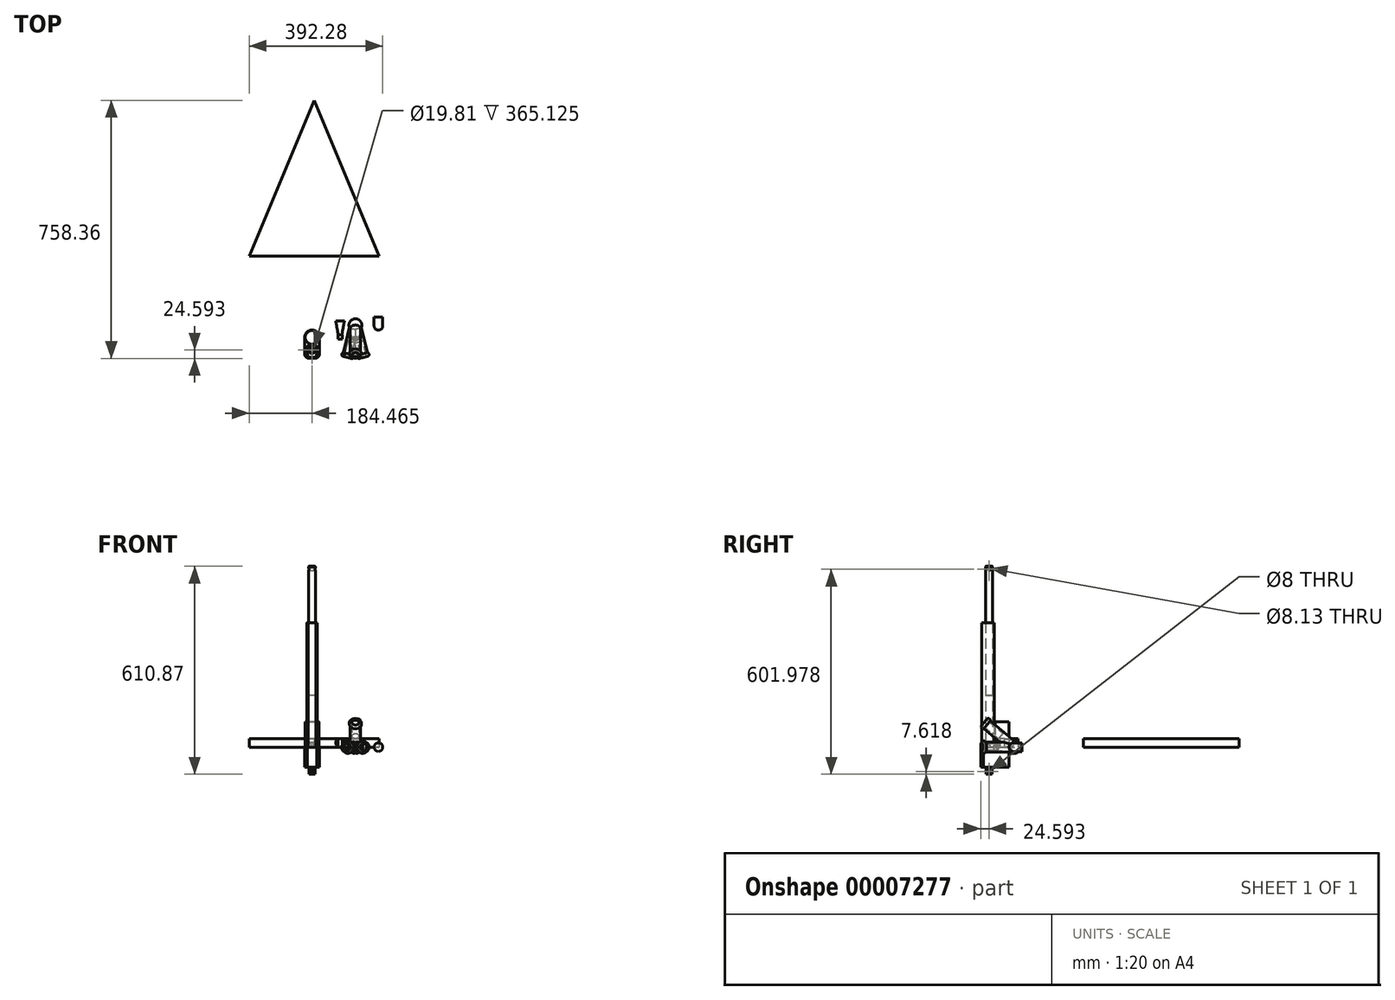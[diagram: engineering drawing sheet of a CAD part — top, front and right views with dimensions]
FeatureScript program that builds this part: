
annotation { "Feature Type Name" : "Feature", "Feature Type Description" : "" }
export const myFeature = defineFeature(function(context is Context, id is Id, definition is map)
    precondition{}
    {
        {
            var Q0;
            Q0=qCreatedBy(makeId("Top.planeOp"),FACE);
            var sketch = newSketch(context, id + "F0", { "sketchPlane" : qUnion([Q0])});
            skLineSegment(sketch, "E0", {"start": v(-190.5, -762.12) * mm, "end": v(0, 0) * mm});
            skLineSegment(sketch, "E1", {"start": v(0, 0) * mm, "end": v(190.5, -762.12) * mm});
            skLineSegment(sketch, "E2", {"start": v(-190.5, -762.12) * mm, "end": v(190.5, -762.12) * mm, "construction": true});
            skPoint(sketch, "E3", {"position": v(0, -762.12) * mm});
            skLineSegment(sketch, "E4.rect.bottom", {"start": v(-48.64, -235.45) * mm, "end": v(-67.86, -230.64) * mm});
            skLineSegment(sketch, "E4.rect.top", {"start": v(-2.54, -51.01) * mm, "end": v(-21.76, -46.2) * mm});
            skLineSegment(sketch, "E4.rect.left", {"start": v(-48.64, -235.45) * mm, "end": v(-2.54, -51.01) * mm});
            skLineSegment(sketch, "E4.rect.right", {"start": v(-67.86, -230.64) * mm, "end": v(-21.76, -46.2) * mm});
            skPoint(sketch, "E4.rect.middle", {"position": v(-35.2, -140.83) * mm});
            skLineSegment(sketch, "E5.rect.bottom", {"start": v(65.5, -221.22) * mm, "end": v(46.29, -226.03) * mm});
            skLineSegment(sketch, "E5.rect.top", {"start": v(21.76, -46.2) * mm, "end": v(2.54, -51.01) * mm});
            skLineSegment(sketch, "E5.rect.left", {"start": v(65.5, -221.22) * mm, "end": v(21.76, -46.2) * mm});
            skLineSegment(sketch, "E5.rect.right", {"start": v(46.29, -226.03) * mm, "end": v(2.54, -51.01) * mm});
            skPoint(sketch, "E5.rect.middle", {"position": v(34.02, -136.12) * mm});
            skCircle(sketch, "E6", {"center": v(0, 0) * mm, "radius": 19.05 * mm});
            skLineSegment(sketch, "E7", {"start": v(-7.7, -92.6) * mm, "end": v(0, -61.8) * mm});
            skLineSegment(sketch, "E8", {"start": v(0, -61.8) * mm, "end": v(7.7, -92.6) * mm});
            skLineSegment(sketch, "E9", {"start": v(-36.78, -85.33) * mm, "end": v(-31.85, -86.56) * mm});
            skLineSegment(sketch, "E10", {"start": v(7.7, -92.6) * mm, "end": v(31.85, -86.56) * mm});
            skLineSegment(sketch, "E11", {"start": v(0, -61.8) * mm, "end": v(0, 0) * mm});
            skLineSegment(sketch, "E12", {"start": v(-3.81, -56.1) * mm, "end": v(1.11, -57.34) * mm});
            skLineSegment(sketch, "E13", {"start": v(8.21, -94.65) * mm, "end": v(13.14, -93.42) * mm, "construction": true});
            skLineSegment(sketch, "E14", {"start": v(36.78, -85.33) * mm, "end": v(17.4, -7.78) * mm});
            skLineSegment(sketch, "E15", {"start": v(-36.78, -85.33) * mm, "end": v(-17.4, -7.78) * mm});
            skLineSegment(sketch, "E16", {"start": v(-25.07, -59.45) * mm, "end": v(-30, -58.22) * mm, "construction": true});
            skLineSegment(sketch, "E17", {"start": v(28.15, -71.75) * mm, "end": v(33.07, -70.52) * mm, "construction": true});
            skLineSegment(sketch, "E18", {"start": v(0, 0) * mm, "end": v(0, 19.05) * mm});
            skCircle(sketch, "E19", {"center": v(-34.31, -85.95) * mm, "radius": 5.71 * mm});
            skCircle(sketch, "E20", {"center": v(34.31, -85.95) * mm, "radius": 5.71 * mm});
            skLineSegment(sketch, "E21", {"start": v(-31.85, -86.56) * mm, "end": v(-7.7, -92.6) * mm});
            skLineSegment(sketch, "E22", {"start": v(31.85, -86.56) * mm, "end": v(36.78, -85.33) * mm});
            skSolve(sketch);
        }
        {
            var Q0;
            Q0=qCreatedBy(makeId("Right.planeOp"),FACE);
            var sketch = newSketch(context, id + "F1", { "sketchPlane" : qUnion([Q0])});
            skLineSegment(sketch, "E23", {"start": v(0, 0) * mm, "end": v(-762.12, 634.6) * mm});
            skLineSegment(sketch, "E24.rect.bottom", {"start": v(-32.7, 40.12) * mm, "end": v(-45.38, 24.9) * mm});
            skLineSegment(sketch, "E24.rect.top", {"start": v(-267.13, 235.32) * mm, "end": v(-279.8, 220.1) * mm});
            skLineSegment(sketch, "E24.rect.left", {"start": v(-45.38, 24.9) * mm, "end": v(-279.8, 220.1) * mm});
            skLineSegment(sketch, "E24.rect.right", {"start": v(-32.7, 40.12) * mm, "end": v(-267.13, 235.32) * mm});
            skPoint(sketch, "E24.rect.middle", {"position": v(-156.25, 130.1) * mm});
            skCircle(sketch, "E25", {"center": v(0, 0) * mm, "radius": 19.05 * mm});
            skLineSegment(sketch, "E26", {"start": v(0, 0) * mm, "end": v(-246.27, 0) * mm, "construction": true});
            skLineSegment(sketch, "E27", {"start": v(0.55, 19.04) * mm, "end": v(-73.42, 80.64) * mm});
            skLineSegment(sketch, "E28", {"start": v(-73.42, 80.64) * mm, "end": v(-76.67, 76.73) * mm});
            skLineSegment(sketch, "E29", {"start": v(-18.63, -4) * mm, "end": v(-92.6, 57.6) * mm});
            skLineSegment(sketch, "E30", {"start": v(-92.6, 57.6) * mm, "end": v(-89.35, 61.5) * mm});
            skCircle(sketch, "E31", {"center": v(-75.05, 78.69) * mm, "radius": 5.72 * mm});
            skSolve(sketch);
        }
        {
            var Q0;
            {var subQ5=sQuery(id+"F0.wireOp",EDGE,"E9");Q0=makeQuery(id+"F0.imprint","IMPRINT",FACE,{"disambiguationData":[TD([[makeQuery(id+"F0.imprint","IMPRINT",EDGE,{"derivedFrom":subQ5}),1.0]])]});}
            var Q1;
            {var subQ5=sQuery(id+"F0.wireOp",EDGE,"E9");Q1=makeQuery(id+"F0.imprint","IMPRINT",FACE,{"disambiguationData":[TD([[makeQuery(id+"F0.imprint","IMPRINT",EDGE,{"derivedFrom":subQ5}),-1.0]])]});}
            var Q2;
            {var subQ7=sQuery(id+"F0.wireOp",EDGE,"E0");var subQ9=sQuery(id+"F0.wireOp",EDGE,"E4.rect.top");var subQ10=makeQuery(id+"F0.imprint","INTERSECT",VERTEX,{"derivedFrom":[subQ7,subQ9]});Q2=makeQuery(id+"F0.imprint","IMPRINT",FACE,{"disambiguationData":[TD([[makeQuery(id+"F0.imprint","IMPRINT",EDGE,{"disambiguationData":[TD([[subQ10,-1.0]])],"derivedFrom":subQ7}),1.0]])]});}
            var Q3;
            {var subQ0=sQuery(id+"F0.wireOp",EDGE,"E18");Q3=makeQuery(id+"F0.imprint","IMPRINT",FACE,{"disambiguationData":[TD([[makeQuery(id+"F0.imprint","IMPRINT",EDGE,{"derivedFrom":subQ0}),1.0]])]});}
            var Q4;
            Q4=sQuery(id+"F0.wireOp",EDGE,"E0");
            revolve(context, id + "F2", {"entities" : qUnion([Q0, Q1, Q2, Q3]), "axis" : qUnion([Q4]), "revolveType" : RevolveType.FULL});
        }
        {
            var Q0;
            {var subQ5=sQuery(id+"F0.wireOp",EDGE,"E22");Q0=makeQuery(id+"F0.imprint","IMPRINT",FACE,{"disambiguationData":[TD([[makeQuery(id+"F0.imprint","IMPRINT",EDGE,{"derivedFrom":subQ5}),-1.0]])]});}
            var Q1;
            {var subQ5=sQuery(id+"F0.wireOp",EDGE,"E22");Q1=makeQuery(id+"F0.imprint","IMPRINT",FACE,{"disambiguationData":[TD([[makeQuery(id+"F0.imprint","IMPRINT",EDGE,{"derivedFrom":subQ5}),1.0]])]});}
            var Q2;
            {var subQ5=sQuery(id+"F0.wireOp",EDGE,"E1");var subQ8=sQuery(id+"F0.wireOp",EDGE,"E6");var subQ9=makeQuery(id+"F0.imprint","INTERSECT",VERTEX,{"derivedFrom":[subQ5,subQ8]});Q2=makeQuery(id+"F0.imprint","IMPRINT",FACE,{"disambiguationData":[TD([[makeQuery(id+"F0.imprint","IMPRINT",EDGE,{"disambiguationData":[TD([[subQ9,-1.0]])],"derivedFrom":subQ5}),1.0]])]});}
            var Q3;
            {var subQ4=sQuery(id+"F0.wireOp",EDGE,"E18");Q3=makeQuery(id+"F0.imprint","IMPRINT",FACE,{"disambiguationData":[TD([[makeQuery(id+"F0.imprint","IMPRINT",EDGE,{"derivedFrom":subQ4}),-1.0]])]});}
            var Q4;
            Q4=sQuery(id+"F0.wireOp",EDGE,"E1");
            revolve(context, id + "F3", {"operationType" : NewBodyOperationType.ADD, "entities" : qUnion([Q0, Q1, Q2, Q3]), "axis" : qUnion([Q4]), "revolveType" : RevolveType.FULL});
        }
        {
            var Q0;
            {var subQ0=sQuery(id+"F1.wireOp",EDGE,"E28");Q0=makeQuery(id+"F1.imprint","IMPRINT",FACE,{"disambiguationData":[TD([[makeQuery(id+"F1.imprint","IMPRINT",EDGE,{"derivedFrom":subQ0}),1.0]])]});}
            var Q1;
            {var subQ5=sQuery(id+"F1.wireOp",EDGE,"E28");Q1=makeQuery(id+"F1.imprint","IMPRINT",FACE,{"disambiguationData":[TD([[makeQuery(id+"F1.imprint","IMPRINT",EDGE,{"derivedFrom":subQ5}),-1.0]])]});}
            var Q2;
            {var subQ5=sQuery(id+"F1.wireOp",EDGE,"E25");var subQ7=sQuery(id+"F1.wireOp",EDGE,"E23");var subQ10=makeQuery(id+"F1.imprint","INTERSECT",VERTEX,{"derivedFrom":[subQ7,subQ5]});Q2=makeQuery(id+"F1.imprint","IMPRINT",FACE,{"disambiguationData":[TD([[makeQuery(id+"F1.imprint","IMPRINT",EDGE,{"disambiguationData":[TD([[subQ10,-1.0]])],"derivedFrom":subQ7}),-1.0]])]});}
            var Q3;
            Q3=sQuery(id+"F1.wireOp",EDGE,"E23");
            revolve(context, id + "F4", {"operationType" : NewBodyOperationType.ADD, "entities" : qUnion([Q0, Q1, Q2]), "axis" : qUnion([Q3]), "revolveType" : RevolveType.FULL});
        }
        {
            var Q0;
            Q0=qCreatedBy(makeId("Top.planeOp"),FACE);
            var sketch = newSketch(context, id + "F5", { "sketchPlane" : qUnion([Q0])});
            skCircle(sketch, "E32", {"center": v(-127.41, -73.1) * mm, "radius": 9.9 * mm});
            skArc(sketch, "E33", {"start": v(-112.6, -76.12) * mm, "mid": v(-127.41, -58) * mm, "end": v(-142.22, -76.12) * mm});
            skLineSegment(sketch, "E34", {"start": v(-138.47, -94.57) * mm, "end": v(-116.36, -94.57) * mm});
            skLineSegment(sketch, "E35", {"start": v(-116.36, -94.57) * mm, "end": v(-112.6, -76.12) * mm});
            skLineSegment(sketch, "E36", {"start": v(-138.47, -94.57) * mm, "end": v(-142.22, -76.12) * mm});
            skSolve(sketch);
        }
        {
            var Q0;
            Q0=makeQuery(id+"F5.imprint","IMPRINT",FACE,{"disambiguationData":[TD([[makeQuery(id+"F5.imprint","IMPRINT",EDGE,{"derivedFrom":sQuery(id+"F5.wireOp",EDGE,"E32")}),1.0]])]});
            extrude(context, id + "F6", {"entities" : qUnion([Q0]), "depth" : 531.37 * mm});
        }
        {
            var Q0;
            Q0=makeQuery(id+"F5.imprint","IMPRINT",FACE,{"disambiguationData":[TD([[makeQuery(id+"F5.imprint","IMPRINT",EDGE,{"derivedFrom":sQuery(id+"F5.wireOp",EDGE,"E32")}),1.0]])]});
            extrude(context, id + "F7", {"entities" : qUnion([Q0]), "operationType" : NewBodyOperationType.REMOVE, "depth" : 152.4 * mm});
        }
        {
            var Q0;
            Q0=qCreatedBy(makeId("Right.planeOp"),FACE);
            var sketch = newSketch(context, id + "F8", { "sketchPlane" : qUnion([Q0])});
            skLineSegment(sketch, "E37", {"start": v(-73.1, 531.37) * mm, "end": v(-73.1, 522.48) * mm, "construction": true});
            skCircle(sketch, "E38", {"center": v(-73.1, 522.48) * mm, "radius": 4.06 * mm});
            skSolve(sketch);
        }
        {
            var Q0;
            Q0=makeQuery(id+"F8.imprint","IMPRINT",FACE,{"disambiguationData":[TD([[makeQuery(id+"F8.imprint","IMPRINT",EDGE,{"derivedFrom":sQuery(id+"F8.wireOp",EDGE,"E38")}),1.0]])]});
            extrude(context, id + "F9", {"entities" : qUnion([Q0]), "operationType" : NewBodyOperationType.REMOVE, "endBound" : BoundingType.THROUGH_ALL, "oppositeDirection" : true, "depth" : 25.4 * mm});
        }
        {
            var Q0;
            Q0=makeQuery(id+"F6.opExtrude","CAP_EDGE",EDGE,{"disambiguationData":[OSD([sQuery(id+"F5.wireOp",EDGE,"E32")])],"isStart":false});
            chamfer(context, id + "F10", {"entities" : qUnion([Q0]), "width" : 1.52 * mm, "tangentPropagation" : true});
        }
        {
            var Q0;
            Q0=makeQuery(id+"F5.imprint","IMPRINT",FACE,{"disambiguationData":[TD([[makeQuery(id+"F5.imprint","IMPRINT",EDGE,{"derivedFrom":sQuery(id+"F5.wireOp",EDGE,"E32")}),-1.0]])]});
            extrude(context, id + "F11", {"entities" : qUnion([Q0]), "depth" : 365.12 * mm});
        }
        {
            var Q0;
            Q0=makeQuery(id+"F11.opExtrude","CAP_FACE",FACE,{"disambiguationData":[OSD([sQuery(id+"F5.wireOp",EDGE,"E32"),sQuery(id+"F5.wireOp",EDGE,"E33"),sQuery(id+"F5.wireOp",EDGE,"E34"),sQuery(id+"F5.wireOp",EDGE,"E35"),sQuery(id+"F5.wireOp",EDGE,"E36")])],"isStart":true});
            var sketch = newSketch(context, id + "F12", { "sketchPlane" : qUnion([Q0])});
            skLineSegment(sketch, "E39", {"start": v(-148.75, 35.51) * mm, "end": v(-148.75, 89.54) * mm});
            skLineSegment(sketch, "E40", {"start": v(-148.75, 89.54) * mm, "end": v(-141.57, 96.73) * mm});
            skLineSegment(sketch, "E41", {"start": v(-141.57, 96.73) * mm, "end": v(-113.26, 96.73) * mm});
            skLineSegment(sketch, "E42", {"start": v(-113.26, 96.73) * mm, "end": v(-106.08, 89.54) * mm});
            skLineSegment(sketch, "E43", {"start": v(-106.08, 89.54) * mm, "end": v(-106.08, 35.51) * mm});
            skLineSegment(sketch, "E44", {"start": v(-148.75, 35.51) * mm, "end": v(-106.08, 35.51) * mm, "construction": true});
            skArc(sketch, "E45", {"start": v(-148.75, 35.51) * mm, "mid": v(-127.41, 14.18) * mm, "end": v(-106.08, 35.51) * mm});
            skLineSegment(sketch, "E46", {"start": v(-136.18, 68.83) * mm, "end": v(-136.18, 77.38) * mm});
            skLineSegment(sketch, "E47", {"start": v(-136.18, 77.38) * mm, "end": v(-131.69, 81.87) * mm});
            skLineSegment(sketch, "E48", {"start": v(-131.69, 81.87) * mm, "end": v(-123.14, 81.87) * mm});
            skLineSegment(sketch, "E49", {"start": v(-123.14, 81.87) * mm, "end": v(-118.65, 77.38) * mm});
            skLineSegment(sketch, "E50", {"start": v(-118.65, 77.38) * mm, "end": v(-118.65, 68.83) * mm});
            skLineSegment(sketch, "E51", {"start": v(-118.65, 68.83) * mm, "end": v(-123.14, 64.34) * mm});
            skLineSegment(sketch, "E52", {"start": v(-123.14, 64.34) * mm, "end": v(-131.69, 64.34) * mm});
            skLineSegment(sketch, "E53", {"start": v(-131.69, 64.34) * mm, "end": v(-136.18, 68.83) * mm});
            skLineSegment(sketch, "E54", {"start": v(-136.18, 73.1) * mm, "end": v(-118.65, 73.1) * mm, "construction": true});
            skPoint(sketch, "E55", {"position": v(-127.41, 73.1) * mm});
            skPoint(sketch, "E56", {"position": v(-127.41, 96.73) * mm});
            skCircle(sketch, "E57", {"center": v(-127.41, 35.51) * mm, "radius": 20.2 * mm});
            skLineSegment(sketch, "E58.0", {"start": v(-141.21, 95.13) * mm, "end": v(-144.96, 76.67) * mm});
            skArc(sketch, "E58.1", {"start": v(-109.87, 76.67) * mm, "mid": v(-127.41, 55.2) * mm, "end": v(-144.96, 76.67) * mm});
            skLineSegment(sketch, "E58.2", {"start": v(-113.62, 95.13) * mm, "end": v(-109.87, 76.67) * mm});
            skLineSegment(sketch, "E59", {"start": v(-113.62, 95.13) * mm, "end": v(-116.36, 94.57) * mm});
            skLineSegment(sketch, "E60", {"start": v(-141.21, 95.13) * mm, "end": v(-138.47, 94.57) * mm});
            skSolve(sketch);
        }
        {
            var Q0;
            Q0=makeQuery(id+"F12.imprint","IMPRINT",FACE,{"disambiguationData":[TD([[makeQuery(id+"F12.imprint","IMPRINT",EDGE,{"derivedFrom":sQuery(id+"F12.wireOp",EDGE,"E39")}),-1.0]])]});
            var Q1;
            Q1=makeQuery(id+"F12.imprint","IMPRINT",FACE,{"disambiguationData":[TD([[makeQuery(id+"F12.imprint","IMPRINT",EDGE,{"derivedFrom":makeQuery(id+"F11.opExtrude","CAP_EDGE",EDGE,{"disambiguationData":[OSD([sQuery(id+"F5.wireOp",EDGE,"E32")])],"isStart":true})}),1.0]])]});
            var Q2;
            Q2=makeQuery(id+"F12.imprint","IMPRINT",FACE,{"disambiguationData":[TD([[makeQuery(id+"F12.imprint","IMPRINT",EDGE,{"derivedFrom":sQuery(id+"F12.wireOp",EDGE,"E46")}),1.0]])]});
            var Q3;
            Q3=makeQuery(id+"F12.imprint","IMPRINT",FACE,{"disambiguationData":[TD([[makeQuery(id+"F12.imprint","IMPRINT",EDGE,{"derivedFrom":sQuery(id+"F12.wireOp",EDGE,"E57")}),1.0]])]});
            var Q4;
            {var subQ5=sQuery(id+"F12.wireOp",EDGE,"E58.0");Q4=makeQuery(id+"F12.imprint","IMPRINT",FACE,{"disambiguationData":[TD([[makeQuery(id+"F12.imprint","IMPRINT",EDGE,{"derivedFrom":subQ5}),1.0]])]});}
            extrude(context, id + "F13", {"entities" : qUnion([Q0, Q1, Q2, Q3, Q4]), "operationType" : NewBodyOperationType.ADD, "depth" : 58.93 * mm});
        }
        {
            var Q0;
            Q0=makeQuery(id+"F12.imprint","IMPRINT",FACE,{"disambiguationData":[TD([[makeQuery(id+"F12.imprint","IMPRINT",EDGE,{"derivedFrom":sQuery(id+"F12.wireOp",EDGE,"E46")}),-1.0]])]});
            extrude(context, id + "F14", {"entities" : qUnion([Q0]), "operationType" : NewBodyOperationType.ADD, "depth" : 79.5 * mm});
        }
        {
            var Q0;
            Q0=makeQuery(id+"F14.opExtrude","SWEPT_FACE",FACE,{"disambiguationData":[OSD([sQuery(id+"F12.wireOp",EDGE,"E50")])]});
            var sketch = newSketch(context, id + "F15", { "sketchPlane" : qUnion([Q0])});
            skCircle(sketch, "E61", {"center": v(-73.1, -71.88) * mm, "radius": 4 * mm});
            skPoint(sketch, "E62", {"position": v(-73.1, -79.5) * mm});
            skSolve(sketch);
        }
        {
            var Q0;
            Q0=makeQuery(id+"F15.imprint","IMPRINT",FACE,{"disambiguationData":[TD([[makeQuery(id+"F15.imprint","IMPRINT",EDGE,{"derivedFrom":sQuery(id+"F15.wireOp",EDGE,"E61")}),1.0]])]});
            extrude(context, id + "F16", {"entities" : qUnion([Q0]), "operationType" : NewBodyOperationType.REMOVE, "oppositeDirection" : true, "depth" : 25.4 * mm});
        }
        {
            var Q0;
            {var subQ5=sQuery(id+"F12.wireOp",EDGE,"E58.0");Q0=makeQuery(id+"F12.imprint","IMPRINT",FACE,{"disambiguationData":[TD([[makeQuery(id+"F12.imprint","IMPRINT",EDGE,{"derivedFrom":subQ5}),1.0]])]});}
            extrude(context, id + "F17", {"entities" : qUnion([Q0]), "operationType" : NewBodyOperationType.ADD, "oppositeDirection" : true, "depth" : 13.46 * mm});
        }
        {
            var Q0;
            {var subQ0=sQuery(id+"F12.wireOp",EDGE,"E58.1");var subQ1=sQuery(id+"F12.wireOp",EDGE,"E57");var subQ3=makeQuery(id+"F12.imprint","INTERSECT",VERTEX,{"disambiguationData":[OD(0.0)],"derivedFrom":[subQ1,subQ0]});Q0=makeQuery(id+"F12.imprint","IMPRINT",FACE,{"disambiguationData":[TD([[makeQuery(id+"F12.imprint","IMPRINT",EDGE,{"disambiguationData":[TD([[subQ3,1.0]])],"derivedFrom":subQ1}),1.0]])]});}
            var Q1;
            {var subQ0=sQuery(id+"F12.wireOp",EDGE,"E58.1");var subQ1=sQuery(id+"F12.wireOp",EDGE,"E57");var subQ3=makeQuery(id+"F12.imprint","INTERSECT",VERTEX,{"disambiguationData":[OD(0.0)],"derivedFrom":[subQ1,subQ0]});Q1=makeQuery(id+"F12.imprint","IMPRINT",FACE,{"disambiguationData":[TD([[makeQuery(id+"F12.imprint","IMPRINT",EDGE,{"disambiguationData":[TD([[subQ3,-1.0]])],"derivedFrom":subQ1}),1.0]])]});}
            extrude(context, id + "F18", {"entities" : qUnion([Q0, Q1]), "operationType" : NewBodyOperationType.ADD, "oppositeDirection" : true, "depth" : 74.68 * mm});
        }
        {
            var Q0;
            Q0=qCreatedBy(makeId("Top.planeOp"),FACE);
            var sketch = newSketch(context, id + "F19", { "sketchPlane" : qUnion([Q0])});
            skLineSegment(sketch, "E63", {"start": v(-311.88, 203.46) * mm, "end": v(69.12, 203.46) * mm});
            skLineSegment(sketch, "E64", {"start": v(69.12, 203.46) * mm, "end": v(-121.38, 660.66) * mm});
            skPoint(sketch, "E64.endSnap0", {"position": v(-121.38, 203.46) * mm});
            skLineSegment(sketch, "E65", {"start": v(-121.38, 660.66) * mm, "end": v(-311.88, 203.46) * mm});
            skSolve(sketch);
        }
        {
            var Q0;
            Q0=makeQuery(id+"F19.imprint","IMPRINT",FACE,{"disambiguationData":[TD([[makeQuery(id+"F19.imprint","IMPRINT",EDGE,{"derivedFrom":sQuery(id+"F19.wireOp",EDGE,"E63")}),1.0]])]});
            extrude(context, id + "F20", {"entities" : qUnion([Q0]), "depth" : 25.4 * mm});
        }
        {
            var Q0;
            Q0=qCreatedBy(makeId("Top.planeOp"),FACE);
            var sketch = newSketch(context, id + "F21", { "sketchPlane" : qUnion([Q0])});
            skCircle(sketch, "E66", {"center": v(-45.03, -37.93) * mm, "radius": 3.18 * mm});
            skLineSegment(sketch, "E67", {"start": v(-57.73, 11.96) * mm, "end": v(-32.33, 11.96) * mm});
            skLineSegment(sketch, "E68", {"start": v(-32.33, 11.96) * mm, "end": v(-41.86, -37.93) * mm});
            skLineSegment(sketch, "E69", {"start": v(-48.2, -37.93) * mm, "end": v(-57.73, 11.96) * mm});
            skLineSegment(sketch, "E70", {"start": v(-41.86, -37.93) * mm, "end": v(-48.2, -37.93) * mm, "construction": true});
            skSolve(sketch);
        }
        {
            var Q0;
            Q0=makeQuery(id+"F21.imprint","IMPRINT",FACE,{"disambiguationData":[TD([[makeQuery(id+"F21.imprint","IMPRINT",EDGE,{"derivedFrom":sQuery(id+"F21.wireOp",EDGE,"E67")}),-1.0]])]});
            var Q1;
            {var subQ0=sQuery(id+"F21.wireOp",EDGE,"E66");var subQ2=makeQuery(id+"F21.imprint","INTERSECT",VERTEX,{"derivedFrom":[subQ0,sQuery(id+"F21.wireOp",EDGE,"E68")]});Q1=makeQuery(id+"F21.imprint","IMPRINT",FACE,{"disambiguationData":[TD([[makeQuery(id+"F21.imprint","IMPRINT",EDGE,{"disambiguationData":[TD([[subQ2,-1.0]])],"derivedFrom":subQ0}),1.0]])]});}
            extrude(context, id + "F22", {"entities" : qUnion([Q0, Q1]), "depth" : 25.4 * mm});
        }
        {
            var Q0;
            Q0=makeQuery(id+"F22.opExtrude","SWEPT_FACE",FACE,{"disambiguationData":[OSD([sQuery(id+"F21.wireOp",EDGE,"E67")])]});
            var sketch = newSketch(context, id + "F23", { "sketchPlane" : qUnion([Q0])});
            skCircle(sketch, "E71", {"center": v(45.03, 12.7) * mm, "radius": 12.7 * mm});
            skLineSegment(sketch, "E72", {"start": v(45.03, 12.7) * mm, "end": v(45.03, 25.4) * mm, "construction": true});
            skSolve(sketch);
        }
        {
            var Q0;
            Q0=qCreatedBy(makeId("Top.planeOp"),FACE);
            var sketch = newSketch(context, id + "F24", { "sketchPlane" : qUnion([Q0])});
            skLineSegment(sketch, "E73", {"start": v(55, -1.75) * mm, "end": v(55, 23.65) * mm});
            skLineSegment(sketch, "E74", {"start": v(55, 23.65) * mm, "end": v(67.7, 23.65) * mm});
            skLineSegment(sketch, "E75", {"start": v(67.7, -1.75) * mm, "end": v(67.7, 23.65) * mm, "construction": true});
            skArc(sketch, "E76", {"start": v(55, -1.75) * mm, "mid": v(58.72, -10.73) * mm, "end": v(67.7, -14.45) * mm});
            skLineSegment(sketch, "E77", {"start": v(67.7, -14.45) * mm, "end": v(67.7, 23.65) * mm});
            skSolve(sketch);
        }
        {
            var Q0;
            Q0=makeQuery(id+"F24.imprint","IMPRINT",FACE,{"disambiguationData":[TD([[makeQuery(id+"F24.imprint","IMPRINT",EDGE,{"derivedFrom":sQuery(id+"F24.wireOp",EDGE,"E73")}),-1.0]])]});
            var Q1;
            Q1=sQuery(id+"F24.wireOp",EDGE,"E77");
            revolve(context, id + "F25", {"entities" : qUnion([Q0]), "axis" : qUnion([Q1]), "revolveType" : RevolveType.FULL});
        }
        {
            var Q0;
            {var subQ0=sQuery(id+"F21.wireOp",EDGE,"E67");var subQ1=makeQuery(id+"F22.opExtrude","CAP_EDGE",EDGE,{"disambiguationData":[OSD([subQ0])],"isStart":false});var subQ2=sQuery(id+"F23.wireOp",EDGE,"E71");var subQ3=makeQuery(id+"F23.imprint","INTERSECT",VERTEX,{"derivedFrom":[subQ1,subQ2]});Q0=makeQuery(id+"F23.imprint","IMPRINT",FACE,{"disambiguationData":[TD([[makeQuery(id+"F23.imprint","IMPRINT",EDGE,{"disambiguationData":[TD([[subQ3,-1.0]])],"derivedFrom":subQ2}),-1.0]])]});}
            var Q1;
            {var subQ0=sQuery(id+"F21.wireOp",EDGE,"E67");var subQ1=makeQuery(id+"F22.opExtrude","CAP_EDGE",EDGE,{"disambiguationData":[OSD([subQ0])],"isStart":false});var subQ2=sQuery(id+"F23.wireOp",EDGE,"E71");var subQ3=makeQuery(id+"F23.imprint","INTERSECT",VERTEX,{"derivedFrom":[subQ1,subQ2]});Q1=makeQuery(id+"F23.imprint","IMPRINT",FACE,{"disambiguationData":[TD([[makeQuery(id+"F23.imprint","IMPRINT",EDGE,{"disambiguationData":[TD([[subQ3,1.0]])],"derivedFrom":subQ2}),-1.0]])]});}
            var Q2;
            {var subQ0=sQuery(id+"F21.wireOp",EDGE,"E67");var subQ1=makeQuery(id+"F22.opExtrude","CAP_EDGE",EDGE,{"disambiguationData":[OSD([subQ0])],"isStart":true});var subQ2=sQuery(id+"F23.wireOp",EDGE,"E71");var subQ3=makeQuery(id+"F23.imprint","INTERSECT",VERTEX,{"derivedFrom":[subQ1,subQ2]});Q2=makeQuery(id+"F23.imprint","IMPRINT",FACE,{"disambiguationData":[TD([[makeQuery(id+"F23.imprint","IMPRINT",EDGE,{"disambiguationData":[TD([[subQ3,1.0]])],"derivedFrom":subQ2}),-1.0]])]});}
            var Q3;
            {var subQ0=sQuery(id+"F21.wireOp",EDGE,"E67");var subQ1=makeQuery(id+"F22.opExtrude","CAP_EDGE",EDGE,{"disambiguationData":[OSD([subQ0])],"isStart":true});var subQ2=sQuery(id+"F23.wireOp",EDGE,"E71");var subQ3=makeQuery(id+"F23.imprint","INTERSECT",VERTEX,{"derivedFrom":[subQ1,subQ2]});Q3=makeQuery(id+"F23.imprint","IMPRINT",FACE,{"disambiguationData":[TD([[makeQuery(id+"F23.imprint","IMPRINT",EDGE,{"disambiguationData":[TD([[subQ3,-1.0]])],"derivedFrom":subQ2}),-1.0]])]});}
            extrude(context, id + "F26", {"entities" : qUnion([Q0, Q1, Q2, Q3]), "operationType" : NewBodyOperationType.REMOVE, "endBound" : BoundingType.THROUGH_ALL, "oppositeDirection" : true, "depth" : 25.4 * mm});
        }
        {
            var Q0;
            Q0=qCreatedBy(makeId("Top.planeOp"),FACE);
            var sketch = newSketch(context, id + "F27", { "sketchPlane" : qUnion([Q0])});
            skLineSegment(sketch, "E78", {"start": v(-51.38, -41.1) * mm, "end": v(-51.38, -28.4) * mm});
            skLineSegment(sketch, "E79", {"start": v(-51.38, -28.4) * mm, "end": v(-38.68, -28.4) * mm});
            skLineSegment(sketch, "E80", {"start": v(-38.68, -28.4) * mm, "end": v(-38.68, -41.1) * mm});
            skLineSegment(sketch, "E81", {"start": v(-38.68, -41.1) * mm, "end": v(-51.38, -41.1) * mm});
            skPoint(sketch, "E82", {"position": v(-45.03, -41.1) * mm});
            skSolve(sketch);
        }
        {
            var Q0;
            Q0=makeQuery(id+"F27.imprint","IMPRINT",FACE,{"disambiguationData":[TD([[makeQuery(id+"F27.imprint","IMPRINT",EDGE,{"derivedFrom":sQuery(id+"F27.wireOp",EDGE,"E78")}),-1.0]])]});
            extrude(context, id + "F28", {"entities" : qUnion([Q0]), "operationType" : NewBodyOperationType.ADD, "depth" : 25.4 * mm});
        }
    });
